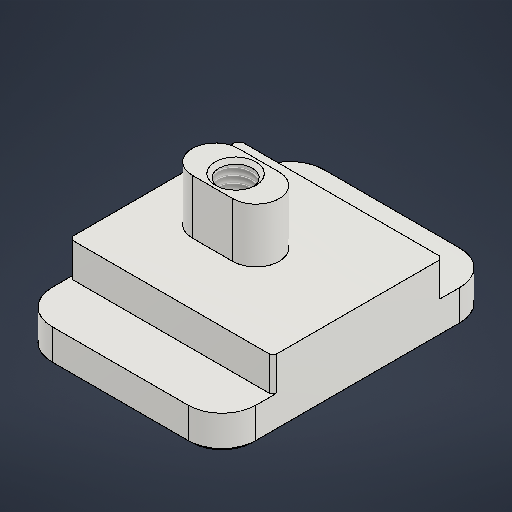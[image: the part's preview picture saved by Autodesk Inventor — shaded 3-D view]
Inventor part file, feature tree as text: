
AUTODESK INVENTOR PART (.ipt)
format: ipt  version: 2025.3 (Build 293356000, 356)  size: 249,344 bytes
history: native  units: mm
features: extrude x4, sketch x2, hole x1, fillet x1, chamfer x1
ambient origin geometry x8: Origin, YZ Plane, XZ Plane, XY Plane, X Axis, Y Axis, Z Axis, Center Point
bodies: Solid1 (feature_tree)
feature tree (9):
  sketch  "Sketch1"  dims[d0=40.0mm d1=30.0mm]
  extrude  "Extrusion1"  Depth=30.0mm
  extrude  "Extrusion2"  Depth=6.8mm
  extrude  "Extrusion5"  Depth=18.0mm
  extrude  "Extrusion6"  TaperAngle=0.0deg  [1 undecoded]
  hole  "Hole1"  [1 undecoded]
  fillet  "Fillet1"  [1 undecoded]
  chamfer  "Chamfer1"  Distance=10.0mm
  sketch  "Sketch3"  dims[d2=6.0mm d3=6.8mm d4=18.0mm d5=0.0mm d6=8.0mm d7=0.0mm d8=4.917mm d9=10.0mm d10=6.0mm d11=2.0mm d12=90.0deg d13=15.0mm d14=0.0mm d15=5.0mm d16=0.5mm d17=2.0mm d18=45.0deg d19=3.0mm d29=15.0mm d30=5.0mm d31=0.0mm d35=25.0mm d36=13.0mm d37=0.0mm]
note: 3 required parameter values undecoded (feature->parameter linkage not recoverable at this tier; creation-order binding heuristic only, values carry confidence <= 0.55)
